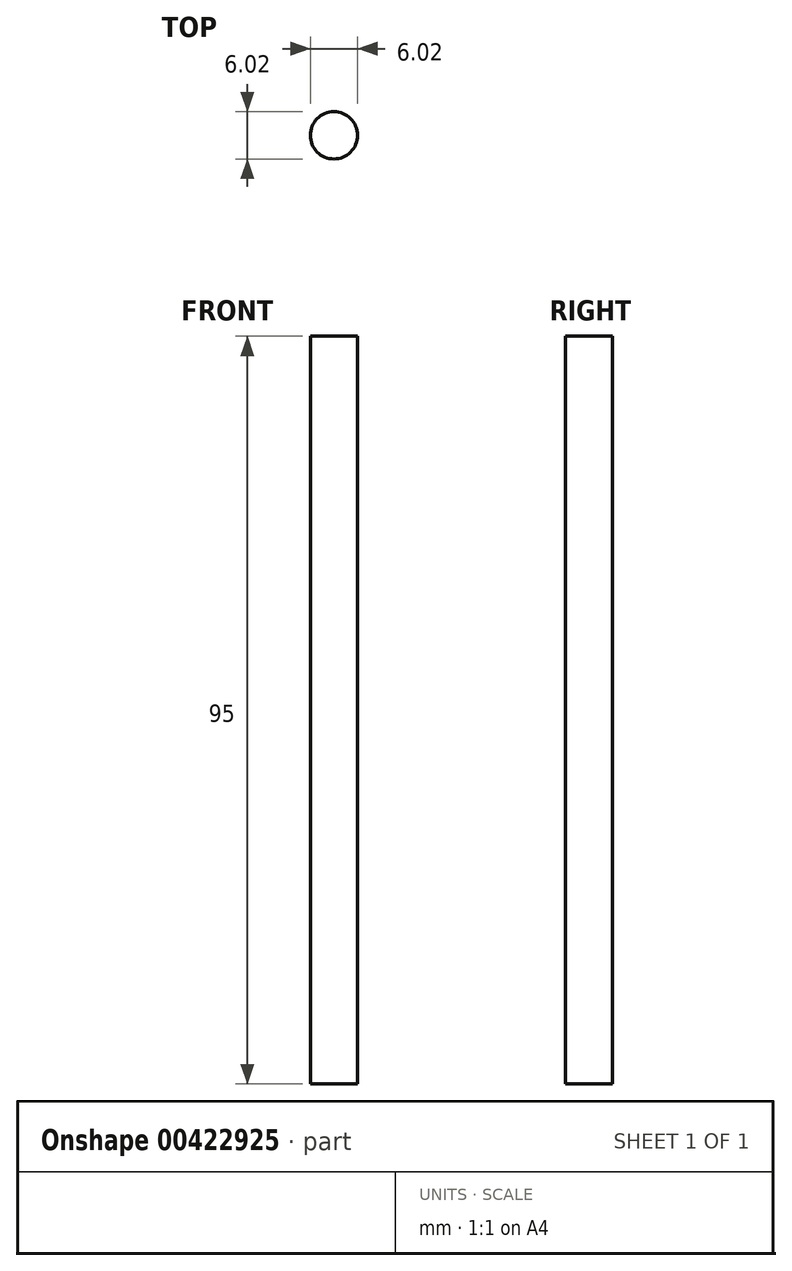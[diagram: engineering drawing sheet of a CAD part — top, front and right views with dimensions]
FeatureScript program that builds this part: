
annotation { "Feature Type Name" : "Feature", "Feature Type Description" : "" }
export const myFeature = defineFeature(function(context is Context, id is Id, definition is map)
    precondition{}
    {
        {
            var Q0;
            Q0=qCreatedBy(makeId("Top.planeOp"),FACE);
            var sketch = newSketch(context, id + "F0", { "sketchPlane" : qUnion([Q0])});
            skCircle(sketch, "E0", {"center": v(0, 0) * mm, "radius": 3 * mm});
            skSolve(sketch);
        }
        {
            var Q0;
            Q0 = qSketchRegion(id + "F0", true);
            extrude(context, id + "F1", {"entities" : qUnion([Q0]), "depth" : 95 * mm});
        }
    });
